# Revit family: l-lego II 110 banner
name_source: partatom
category: Осветительные приборы
revit_build: Autodesk Revit 2017 (Build: 20160225_1515(x64)
units: mm (PartAtom-declared; Revit-internal decimal feet)

## family parameters
Источник света = Да
Общий = Нет
Основа = Грань
При загрузке вырезать с полостями = Нет
Размер круглого соединителя = Использовать диаметр
Тип детали = Нормальный
Точка расчета площади = Нет

## types (8) — shared parameters
L = 157 мм
Видимая форма излучения при визуализации = Нет
Изготовитель = LEDEL
Излучение по длине прямоугольника = 100 мм
Излучение по ширине прямоугольника = 100 мм
Комментарии к типоразмеру = Прожекторы
Отметка по умолчанию = 1219 мм
Полная установленная мощность = 90 В·А
Светофильтр = 16777215
Смещение цветовой температуры при затухании лампы = <Нет>

## per-type parameters (varying)
| type | Артикул | Угол наклона | Файл фотометрической сетки |
| L-lego II 110 banner-90-D-5.0K | LII039 | 90.00° | L-lego 110 banner-90-D-5.0K-01.ies |
| L-lego II 110 banner-90-G30-5.0K | LII035 | 90.00° | L-lego 110 banner-90-G30-5.0K-01.ies |
| L-lego II 110 banner-90-G60-5.0K | LII037 | 90.00° | L-lego 110 banner-90-G60-5.0K-01.ies |
| L-lego II 110 banner-90-K15-5.0K | LII041 | -90.00° | L-lego 110 banner-90-K15-5.0K-01.ies |
| L-lego II 110 banner-90-K15-4.0K | LII040 | -90.00° | L-lego 110 banner-90-K15-5.0K-01.ies |
| L-lego II 110 banner-90-D-4.0K | LII038 | 90.00° | L-lego 110 banner-90-D-5.0K-01.ies |
| L-lego II 110 banner-90-G30-4.0K | LII034 | 90.00° | L-lego 110 banner-90-G30-5.0K-01.ies |
| L-lego II 110 banner-90-G60-4.0K | LII036 | -90.00° | L-lego 110 banner-90-G60-5.0K-01.ies |

## geometry (parser evidence)
native form markers: Sweep x2
no freeform markers — native parametric forms only
